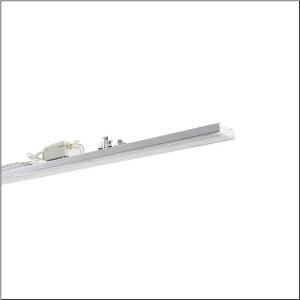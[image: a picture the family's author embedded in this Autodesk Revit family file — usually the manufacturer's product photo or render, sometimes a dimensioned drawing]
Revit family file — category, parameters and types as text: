
# Revit family: licross_11_recessed_mo_51tl117n485g
name_source: partatom
category: Lighting Fixtures
units: mm (PartAtom-declared; Revit-internal decimal feet)

## family parameters
Cut with Voids When Loaded = No
Host = Face
Light Source = No
Part Type = Normal
Room Calculation Point = No
Round Connector Dimension = Use Diameter
Shared = No

## types (1)
- Licross 11 Recessed MO (1 x LED, 8810 lm, 48.5 W, 4000K)
    Apparent Load = 49 VA
    CIE Flux Codes = 89 96 99 100 100
    Color Rendering = 80
    Color Temperature = 4000K
    Default Elevation = 1800 mm
    Description = Licross 11 Recessed MO, luminaire insert, of sheet steel, coil coated, white, length: 1.500mm, width: 66mm, height: 67mm, LED rated luminous flux: 8.820lm, light colour: 840, SDCM (Standard Deviation of Colour Matching)MacAdam ≤ 2 SDCM (initial), control gear: ON/OFF, with plug, 3-pole, with phase selection, mains connection: 220..240V, AC, 50/60Hz, rated input power: 49W, internal wiring halogen-free, primary light control with lens, of plastic, primary optical cover: cover, of PMMA, light emission: direct distribution, primary light characteristic: symmetric, protection rating (complete): IP40, insulation class (complete): insulation class I (protective earthing), certification: CE, ENEC, VDE, UKCA, protection symbol: D if used in an environment without relevant dust loads with corresponding accessories, impact resistance: IK06, permissible ambient temperature for indoor applications: -35..+35°C, corresponds to IFS (International Featured Standards) requirements for safety and quality in the food industry, reducing of maximum allowable ambient temperature of 5°C with ceiling mounting, The light source and the operating device comply with the requirements of the Ecodesign Regulation (EU) 2019/2020 and are replaceable in accordance with this regulation, packaging unit: 1 piece
    Height = 58 mm
    Lamp = 1 x LED
    Lamp Light Flux = 8810 lm
    Lamp Power = 48.5 W
    Lamp count = 1
    Length = 1500 mm
    Luminous efficacy = 182 lm/W
    Manufacturer = Siteco
    ModVariant = No
    Model = 51TL117N485G
    Mounting Place = Ceiling
    Mounting Type = Pendant
    Number of Poles = 1
    OnlyDefault = Yes
    Power Factor = 1
    Product Name = Licross 11 Recessed MO
    Product group = luminaire insert | ceiling pendant
    ProductGroupID = 901
    Protection Class = Protection class I
    Protection Degree = IP 40
    RLX_Detail_Level = 1
    RLX_Emergency_Light_Flux = 0 lm
    RLX_Emergency_Type = 0
    RLX_Emergency_Type_DB = No
    RlxData = <blob elided: 21065 chars, md5=ac029eac>
    Socket = socket
    Standby Power = 0 W
    System Light Flux = 8810 lm
    System Power = 49 W
    Type Comments = Product without accessories
    Type Image = l_1296930.jpg
    URL = http://relux.com
    VarID = ---
    Voltage = 0 V
    Weight = 0.00 kg
    Width = 66 mm

## geometry (parser evidence)
native form markers: Blend x4, Sweep x12
no freeform markers — native parametric forms only
